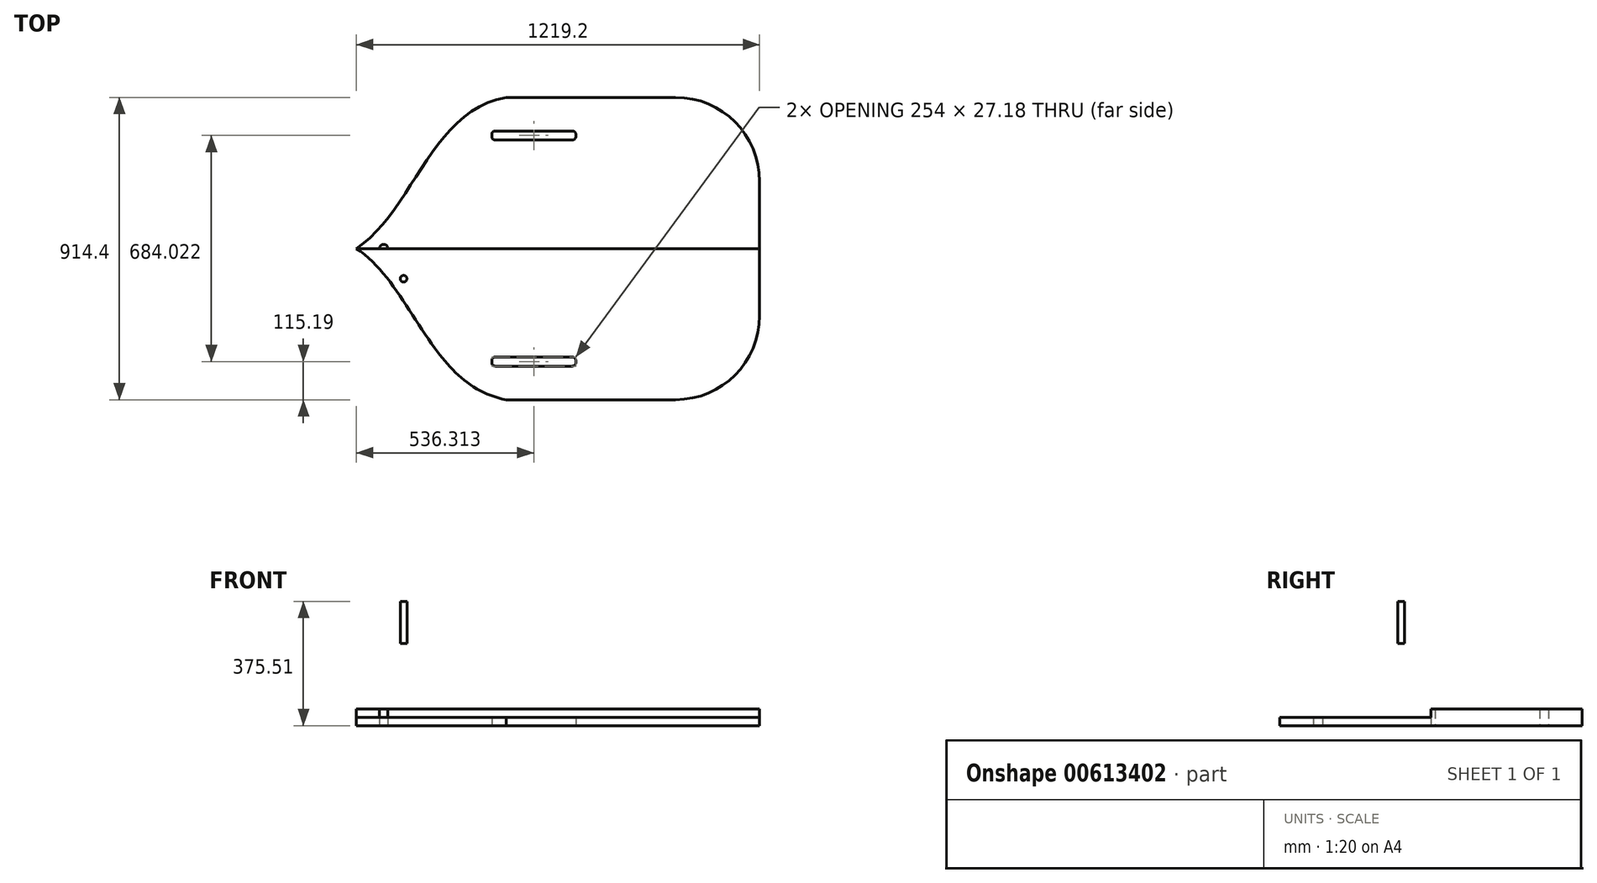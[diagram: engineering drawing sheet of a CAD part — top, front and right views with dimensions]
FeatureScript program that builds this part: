
annotation { "Feature Type Name" : "Feature", "Feature Type Description" : "" }
export const myFeature = defineFeature(function(context is Context, id is Id, definition is map)
    precondition{}
    {
        {
            var Q0;
            Q0=qCreatedBy(makeId("Top.planeOp"),FACE);
            var sketch = newSketch(context, id + "F0", { "sketchPlane" : qUnion([Q0])});
            skLineSegment(sketch, "E0.bottom", {"start": v(0, 548.5) * mm, "end": v(512.74, 548.5) * mm});
            skLineSegment(sketch, "E0.top", {"start": v(0, -365.9) * mm, "end": v(512.74, -365.9) * mm});
            skLineSegment(sketch, "E0.right", {"start": v(766.74, 294.5) * mm, "end": v(766.74, -111.9) * mm});
            skPoint(sketch, "E1", {"position": v(-452.46, 91.3) * mm});
            skLineSegment(sketch, "E2", {"start": v(-452.46, 91.3) * mm, "end": v(766.74, 91.3) * mm});
            skLineSegment(sketch, "E3", {"start": v(461.94, 548.5) * mm, "end": v(461.94, -365.9) * mm, "construction": true});
            skPoint(sketch, "E4.visualSharp", {"position": v(766.74, -365.9) * mm});
            skArc(sketch, "E4.filletArc", {"start": v(512.74, -365.9) * mm, "mid": v(692.34, -291.51) * mm, "end": v(766.74, -111.9) * mm});
            skPoint(sketch, "E5.visualSharp", {"position": v(766.74, 548.5) * mm});
            skArc(sketch, "E5.filletArc", {"start": v(766.74, 294.5) * mm, "mid": v(692.34, 474.1) * mm, "end": v(512.74, 548.5) * mm});
            skLineSegment(sketch, "E6", {"start": v(-214.96, -210.66) * mm, "end": v(945.31, -210.66) * mm});
            skLineSegment(sketch, "E7.MirrorCS", {"start": v(-110.25, 393.24) * mm, "end": v(945.31, 393.24) * mm});
            skLineSegment(sketch, "E8", {"start": v(210.85, -254.15) * mm, "end": v(210.85, -247.3) * mm});
            skLineSegment(sketch, "E9", {"start": v(200.7, -237.13) * mm, "end": v(-32.99, -237.13) * mm});
            skLineSegment(sketch, "E10", {"start": v(-43.15, -247.3) * mm, "end": v(-43.15, -254.15) * mm});
            skLineSegment(sketch, "E11", {"start": v(-32.99, -264.3) * mm, "end": v(200.7, -264.3) * mm});
            skPoint(sketch, "E12.orphan", {"position": v(210.85, -345.27) * mm});
            skPoint(sketch, "E13.visualSharp", {"position": v(-43.15, -237.13) * mm});
            skArc(sketch, "E13.filletArc", {"start": v(-32.99, -237.13) * mm, "mid": v(-40.17, -240.1) * mm, "end": v(-43.15, -247.3) * mm});
            skPoint(sketch, "E14.visualSharp", {"position": v(-43.15, -264.3) * mm});
            skArc(sketch, "E14.filletArc", {"start": v(-43.15, -254.15) * mm, "mid": v(-40.17, -261.33) * mm, "end": v(-32.99, -264.3) * mm});
            skPoint(sketch, "E15.visualSharp", {"position": v(210.85, -237.13) * mm});
            skArc(sketch, "E15.filletArc", {"start": v(210.85, -247.3) * mm, "mid": v(207.88, -240.1) * mm, "end": v(200.7, -237.13) * mm});
            skPoint(sketch, "E16.visualSharp", {"position": v(210.85, -264.3) * mm});
            skArc(sketch, "E16.filletArc", {"start": v(200.7, -264.3) * mm, "mid": v(207.88, -261.33) * mm, "end": v(210.85, -254.15) * mm});
            skLineSegment(sketch, "E17.MirrorCS", {"start": v(200.7, 419.71) * mm, "end": v(-32.99, 419.71) * mm});
            skLineSegment(sketch, "E18.MirrorCS", {"start": v(-32.99, 446.9) * mm, "end": v(200.7, 446.9) * mm});
            skArc(sketch, "E19.MirrorCS", {"start": v(210.85, 429.87) * mm, "mid": v(207.88, 422.69) * mm, "end": v(200.7, 419.71) * mm});
            skArc(sketch, "E20.MirrorCS", {"start": v(-32.99, 419.71) * mm, "mid": v(-40.17, 422.69) * mm, "end": v(-43.15, 429.87) * mm});
            skArc(sketch, "E21.MirrorCS", {"start": v(-43.15, 436.73) * mm, "mid": v(-40.17, 443.92) * mm, "end": v(-32.99, 446.9) * mm});
            skLineSegment(sketch, "E22.MirrorCS", {"start": v(210.85, 436.73) * mm, "end": v(210.85, 429.87) * mm});
            skLineSegment(sketch, "E23.MirrorCS", {"start": v(-43.15, 429.87) * mm, "end": v(-43.15, 436.73) * mm});
            skArc(sketch, "E24", {"start": v(210.85, 436.73) * mm, "mid": v(207.88, 443.92) * mm, "end": v(200.7, 446.9) * mm});
            skPoint(sketch, "E25.orphan", {"position": v(-325.05, 393.24) * mm});
            skPoint(sketch, "E26", {"position": v(-110.25, 393.24) * mm});
            skFitSpline(sketch, "E27", {"points": [v(-452.46, 91.3) * mm, v(0, 548.5) * mm], "startDerivative": vector(508.6, 333.03) * mm, "endDerivative": vector(681.85, 123.73) * mm});
            skFitSpline(sketch, "E28.MirrorCS", {"points": [v(-452.46, 91.3) * mm, v(0, -365.9) * mm], "startDerivative": vector(508.6, -333.03) * mm, "endDerivative": vector(681.85, -123.73) * mm});
            skCircle(sketch, "E29", {"center": v(-370, 91.3) * mm, "radius": 12.7 * mm});
            skLineSegment(sketch, "E30", {"start": v(-364.76, 102.86) * mm, "end": v(-370, 91.3) * mm});
            skLineSegment(sketch, "E31", {"start": v(-370, 91.3) * mm, "end": v(-214.96, 91.3) * mm});
            skSolve(sketch);
        }
        {
            var Q0;
            {var subQ0=sQuery(id+"F0.wireOp",EDGE,"E0.bottom");Q0=makeQuery(id+"F0.imprint","IMPRINT",FACE,{"disambiguationData":[TD([[makeQuery(id+"F0.imprint","IMPRINT",EDGE,{"derivedFrom":subQ0}),-1.0]])]});}
            var Q1;
            {var subQ0=sQuery(id+"F0.wireOp",EDGE,"E0.top");Q1=makeQuery(id+"F0.imprint","IMPRINT",FACE,{"disambiguationData":[TD([[makeQuery(id+"F0.imprint","IMPRINT",EDGE,{"derivedFrom":subQ0}),1.0]])]});}
            var Q2;
            {var subQ6=sQuery(id+"F0.wireOp",EDGE,"E2");Q2=makeQuery(id+"F0.imprint","IMPRINT",FACE,{"disambiguationData":[TD([[makeQuery(id+"F0.imprint","IMPRINT",EDGE,{"derivedFrom":subQ6}),-1.0]])]});}
            extrude(context, id + "F1", {"entities" : qUnion([Q0, Q1, Q2]), "depth" : 25.4 * mm, "offsetDistance" : 25.4 * mm});
        }
        {
            var Q0;
            Q0=qSketchRegion(id+"F0",true);
            var Q1;
            Q1=makeQuery(id+"F1.opExtrude","CAP_FACE",FACE,{"disambiguationData":[OSD([sQuery(id+"F0.wireOp",EDGE,"E0.bottom"),sQuery(id+"F0.wireOp",EDGE,"E0.top"),sQuery(id+"F0.wireOp",EDGE,"E0.right"),sQuery(id+"F0.wireOp",EDGE,"E2"),sQuery(id+"F0.wireOp",EDGE,"E4.filletArc"),sQuery(id+"F0.wireOp",EDGE,"E5.filletArc"),sQuery(id+"F0.wireOp",EDGE,"E8"),sQuery(id+"F0.wireOp",EDGE,"E9"),sQuery(id+"F0.wireOp",EDGE,"E10"),sQuery(id+"F0.wireOp",EDGE,"E11"),sQuery(id+"F0.wireOp",EDGE,"E13.filletArc"),sQuery(id+"F0.wireOp",EDGE,"E14.filletArc"),sQuery(id+"F0.wireOp",EDGE,"E15.filletArc"),sQuery(id+"F0.wireOp",EDGE,"E16.filletArc"),sQuery(id+"F0.wireOp",EDGE,"E17.MirrorCS"),sQuery(id+"F0.wireOp",EDGE,"E18.MirrorCS"),sQuery(id+"F0.wireOp",EDGE,"E20.MirrorCS"),sQuery(id+"F0.wireOp",EDGE,"E21.MirrorCS"),sQuery(id+"F0.wireOp",EDGE,"E22.MirrorCS"),sQuery(id+"F0.wireOp",EDGE,"E23.MirrorCS"),sQuery(id+"F0.wireOp",EDGE,"E19.MirrorCS"),sQuery(id+"F0.wireOp",EDGE,"E24"),sQuery(id+"F0.wireOp",EDGE,"E27"),sQuery(id+"F0.wireOp",EDGE,"E28.MirrorCS"),sQuery(id+"F0.wireOp",EDGE,"E29")])],"isStart":false});
            extrude(context, id + "F2", {"entities" : qUnion([Q0, Q1]), "operationType" : NewBodyOperationType.ADD, "depth" : 25.4 * mm, "offsetDistance" : 25.4 * mm});
        }
        {
            var Q0;
            Q0=qCreatedBy(makeId("Front.planeOp"),FACE);
            var sketch = newSketch(context, id + "F3", { "sketchPlane" : qUnion([Q0])});
            skLineSegment(sketch, "E32.bottom", {"start": v(-309.94, 248.5) * mm, "end": v(-320.1, 248.5) * mm});
            skLineSegment(sketch, "E32.top", {"start": v(-309.94, 375.5) * mm, "end": v(-320.1, 375.5) * mm});
            skLineSegment(sketch, "E32.left", {"start": v(-309.94, 248.5) * mm, "end": v(-309.94, 375.5) * mm});
            skLineSegment(sketch, "E32.right", {"start": v(-320.1, 248.5) * mm, "end": v(-320.1, 375.5) * mm});
            skPoint(sketch, "E32.middle", {"position": v(-315.02, 312) * mm});
            skSolve(sketch);
        }
        {
            var Q0;
            Q0=makeQuery(id+"F3.imprint","IMPRINT",FACE,{"disambiguationData":[TD([[makeQuery(id+"F3.imprint","IMPRINT",EDGE,{"derivedFrom":sQuery(id+"F3.wireOp",EDGE,"E32.bottom")}),-1.0]])]});
            var Q1;
            Q1=sQuery(id+"F3.wireOp",EDGE,"E32.left");
            revolve(context, id + "F4", {"entities" : qUnion([Q0]), "axis" : qUnion([Q1]), "revolveType" : RevolveType.FULL});
        }
    });
